# Revit family: QF_BOURGEAT_Lave_mains_eco_responsable_Modèles_sur_secteur
name_source: partatom
category: Appareils sanitaires
revit_build: Autodesk Revit 2015 (Build: 20140606_1530(x64)
units: mm (PartAtom-declared; Revit-internal decimal feet)

## types (8) — shared parameters
Capacité de la cuve = 3 L
Consommation  d'eau Froide = 0.0 L/s
Diamètre de Raccordement Eau Adoucie = 21 mm
Diamètre de Raccordement Evacuation = 32 mm
Débit Eau Adoucie = 0.2 L/s
Fabricant = BOURGEAT
Fréquence = 50 Hz
Hauteur de la cuve = 72 mm  [stored 0.23622 ft]
Hauteur hors tout = 403 mm  [stored 1.32218 ft]
Indice de protection = 24
Largeur de la cuve = 260 mm  [stored 0.853018 ft]
Longueur de la cuve = 380 mm
Longueur hors tout = 395 mm  [stored 1.29593 ft]
Phase = 2
Poids net à vide = 5.00 kg
Poids à vide = 5 kg
Puissance éléctrique (à suppr) = 24 W
Spécification du Fabricant = Lave mains écoresponsable sur secteur
URL catalogue = http://www.bourgeat.fr
zero-valued in all types: Hauteur de Raccordement Eau Adoucie du Sol Finis

## per-type parameters (varying)
| type | Angle droit | Intensité nominale | Modèle | Mur plan | Profondeur hors tout | Puissance électrique  | Tension |
| Fixation sur mur plan avec mélangeur | Non | 1 A | 852011 | Oui | 388 mm  [stored 1.27297 ft] | 24 W | 240 V |
| Fixation sur mur plan sans mélangeur | Non | 1 A | 852001 | Oui | 388 mm  [stored 1.27297 ft] | 24 W | 240 V |
| Fixation sur mur à angle droit avec mélangeur | Oui | 1 A | 852012 | Non | 411 mm  [stored 1.34843 ft] | 24 W | 240 V |
| Fixation sur mur à angle droit sans mélangeur | Oui | 1 A | 852002 | Non | 411 mm  [stored 1.34843 ft] | 24 W | 240 V |
| Fixation sur mur plan sans mélangeur avec chauffe eau | Non | 4 A | 852001 | Oui | 388 mm  [stored 1.27297 ft] | 824 W | 230 V |
| Fixation sur mur plan avec mélangeur avec chauffe eau | Non | 4 A | 852011 | Oui | 388 mm  [stored 1.27297 ft] | 824 W | 230 V |
| Fixation sur mur à angle droit sans mélangeur avec chauffe eau | Oui | 4 A | 852002 | Non | 411 mm  [stored 1.34843 ft] | 824 W | 240 V |
| Fixation sur mur à angle droit avec mélangeur avec chauffe eau | Oui | 4 A | 852012 | Non | 411 mm  [stored 1.34843 ft] | 824 W | 240 V |

note: [stored X ft] marks values corroborated as IEEE doubles in the binary element streams (Revit-internal decimal feet)
